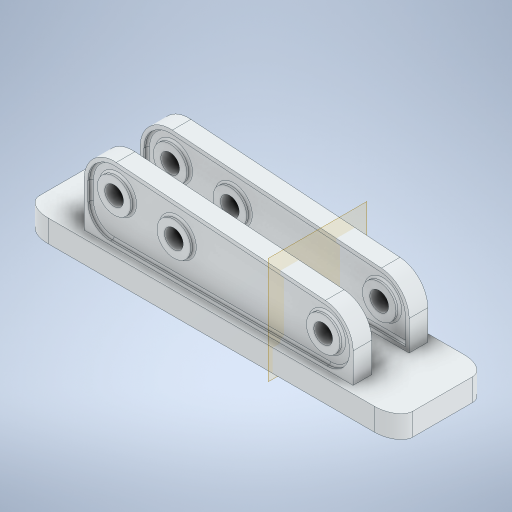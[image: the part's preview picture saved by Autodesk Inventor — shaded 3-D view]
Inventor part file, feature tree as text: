
AUTODESK INVENTOR PART (.ipt)
format: ipt  version: 2024 (Build 280153000, 153)  size: 414,208 bytes
history: native  units: in
note: dims shown in document units (in); Inventor stores cm internally (conversion verified against a paired STEP export)
features: sketch x5, plane x1
ambient origin geometry x8: Origin, YZ Plane, XZ Plane, XY Plane, X Axis, Y Axis, Z Axis, Center Point
bodies: Solid1 (feature_tree), Body1 (feature_tree)
feature tree (6):
  sketch  "Sketch1"  dims[d0=8.3125in]
  sketch  "Sketch2"
  plane  "Work Plane1"
  sketch  "Sketch3"
  sketch  "Sketch4"
  sketch  "Sketch5"
